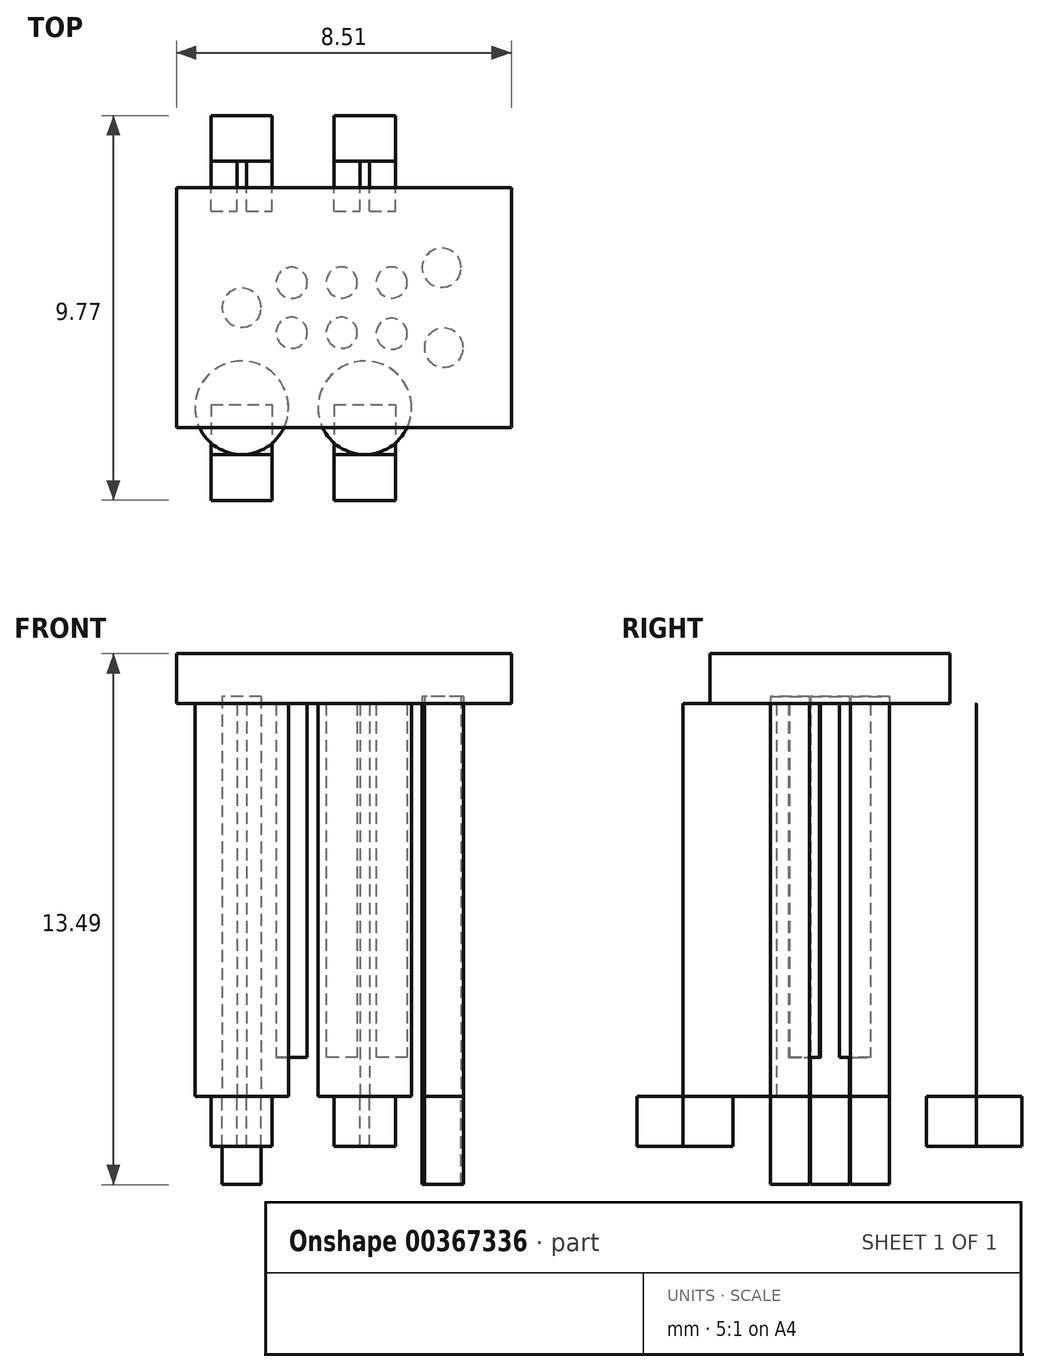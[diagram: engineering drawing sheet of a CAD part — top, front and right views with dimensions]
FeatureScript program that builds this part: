
annotation { "Feature Type Name" : "Feature", "Feature Type Description" : "" }
export const myFeature = defineFeature(function(context is Context, id is Id, definition is map)
    precondition{}
    {
        {
            var Q0;
            Q0=qCreatedBy(makeId("Top.planeOp"),FACE);
            var sketch = newSketch(context, id + "F0", { "sketchPlane" : qUnion([Q0])});
            skCircle(sketch, "E0", {"center": v(0, 0) * mm, "radius": 0.5 * mm});
            skCircle(sketch, "E1", {"center": v(5.13, -1.02) * mm, "radius": 0.5 * mm});
            skCircle(sketch, "E2", {"center": v(5.08, 1.02) * mm, "radius": 0.5 * mm});
            skCircle(sketch, "E3", {"center": v(1.27, 0.64) * mm, "radius": 0.4 * mm});
            skCircle(sketch, "E4", {"center": v(1.27, -0.63) * mm, "radius": 0.4 * mm});
            skCircle(sketch, "E5", {"center": v(2.54, 0.64) * mm, "radius": 0.4 * mm});
            skCircle(sketch, "E6", {"center": v(2.54, -0.63) * mm, "radius": 0.4 * mm});
            skCircle(sketch, "E7", {"center": v(3.81, 0.64) * mm, "radius": 0.4 * mm});
            skCircle(sketch, "E8", {"center": v(3.81, -0.66) * mm, "radius": 0.4 * mm});
            skCircle(sketch, "E9", {"center": v(0, 2.54) * mm, "radius": 1.19 * mm});
            skCircle(sketch, "E10", {"center": v(3.13, 2.54) * mm, "radius": 1.19 * mm});
            skCircle(sketch, "E11", {"center": v(0, -2.54) * mm, "radius": 1.19 * mm});
            skCircle(sketch, "E12", {"center": v(3.13, -2.54) * mm, "radius": 1.19 * mm});
            skLineSegment(sketch, "E13.bottom", {"start": v(-0.77, 4.88) * mm, "end": v(0.77, 4.88) * mm});
            skLineSegment(sketch, "E13.top", {"start": v(-0.77, 3.72) * mm, "end": v(0.77, 3.72) * mm});
            skLineSegment(sketch, "E13.left", {"start": v(-0.77, 4.88) * mm, "end": v(-0.77, 3.72) * mm});
            skLineSegment(sketch, "E13.right", {"start": v(0.77, 4.88) * mm, "end": v(0.77, 3.72) * mm});
            skLineSegment(sketch, "E14.bottom", {"start": v(2.35, 4.88) * mm, "end": v(3.9, 4.88) * mm});
            skLineSegment(sketch, "E14.top", {"start": v(2.35, 3.72) * mm, "end": v(3.9, 3.72) * mm});
            skLineSegment(sketch, "E14.left", {"start": v(2.35, 4.88) * mm, "end": v(2.35, 3.72) * mm});
            skLineSegment(sketch, "E14.right", {"start": v(3.9, 4.88) * mm, "end": v(3.9, 3.72) * mm});
            skLineSegment(sketch, "E15.bottom", {"start": v(-0.77, -3.73) * mm, "end": v(0.77, -3.73) * mm});
            skLineSegment(sketch, "E15.top", {"start": v(-0.77, -4.9) * mm, "end": v(0.77, -4.9) * mm});
            skLineSegment(sketch, "E15.left", {"start": v(-0.77, -3.73) * mm, "end": v(-0.77, -4.9) * mm});
            skLineSegment(sketch, "E15.right", {"start": v(0.77, -3.73) * mm, "end": v(0.77, -4.9) * mm});
            skLineSegment(sketch, "E16.bottom", {"start": v(2.35, -3.73) * mm, "end": v(3.9, -3.73) * mm});
            skLineSegment(sketch, "E16.top", {"start": v(2.35, -4.9) * mm, "end": v(3.9, -4.9) * mm});
            skLineSegment(sketch, "E16.left", {"start": v(2.35, -3.73) * mm, "end": v(2.35, -4.9) * mm});
            skLineSegment(sketch, "E16.right", {"start": v(3.9, -3.73) * mm, "end": v(3.9, -4.9) * mm});
            skSolve(sketch);
        }
        {
            var Q0;
            Q0=makeQuery(id+"F0.imprint","IMPRINT",FACE,{"disambiguationData":[TD([[makeQuery(id+"F0.imprint","IMPRINT",EDGE,{"derivedFrom":sQuery(id+"F0.wireOp",EDGE,"E13.bottom")}),-1.0]])]});
            var Q1;
            Q1=makeQuery(id+"F0.imprint","IMPRINT",FACE,{"disambiguationData":[TD([[makeQuery(id+"F0.imprint","IMPRINT",EDGE,{"derivedFrom":sQuery(id+"F0.wireOp",EDGE,"E14.bottom")}),-1.0]])]});
            var Q2;
            Q2=makeQuery(id+"F0.imprint","IMPRINT",FACE,{"disambiguationData":[TD([[makeQuery(id+"F0.imprint","IMPRINT",EDGE,{"derivedFrom":sQuery(id+"F0.wireOp",EDGE,"E15.bottom")}),-1.0]])]});
            var Q3;
            Q3=makeQuery(id+"F0.imprint","IMPRINT",FACE,{"disambiguationData":[TD([[makeQuery(id+"F0.imprint","IMPRINT",EDGE,{"derivedFrom":sQuery(id+"F0.wireOp",EDGE,"E16.bottom")}),-1.0]])]});
            extrude(context, id + "F1", {"entities" : qUnion([Q0, Q1, Q2, Q3]), "depth" : -1.27 * mm});
        }
        {
            var Q0;
            Q0=makeQuery(id+"F0.imprint","IMPRINT",FACE,{"disambiguationData":[TD([[makeQuery(id+"F0.imprint","IMPRINT",EDGE,{"derivedFrom":sQuery(id+"F0.wireOp",EDGE,"E1")}),1.0]])]});
            var Q1;
            Q1=makeQuery(id+"F0.imprint","IMPRINT",FACE,{"disambiguationData":[TD([[makeQuery(id+"F0.imprint","IMPRINT",EDGE,{"derivedFrom":sQuery(id+"F0.wireOp",EDGE,"E2")}),1.0]])]});
            var Q2;
            Q2=makeQuery(id+"F0.imprint","IMPRINT",FACE,{"disambiguationData":[TD([[makeQuery(id+"F0.imprint","IMPRINT",EDGE,{"derivedFrom":sQuery(id+"F0.wireOp",EDGE,"E0")}),1.0]])]});
            extrude(context, id + "F2", {"entities" : qUnion([Q0, Q1, Q2]), "depth" : -2.24 * mm});
        }
        {
            var Q0;
            Q0=makeQuery(id+"F0.imprint","IMPRINT",FACE,{"disambiguationData":[TD([[makeQuery(id+"F0.imprint","IMPRINT",EDGE,{"derivedFrom":sQuery(id+"F0.wireOp",EDGE,"E11")}),1.0]])]});
            var Q1;
            Q1=makeQuery(id+"F0.imprint","IMPRINT",FACE,{"disambiguationData":[TD([[makeQuery(id+"F0.imprint","IMPRINT",EDGE,{"derivedFrom":sQuery(id+"F0.wireOp",EDGE,"E12")}),1.0]])]});
            var Q2;
            {var subQ0=sQuery(id+"F0.wireOp",EDGE,"E14.top");var subQ1=sQuery(id+"F0.wireOp",EDGE,"E10");var subQ2=makeQuery(id+"F0.imprint","INTERSECT",VERTEX,{"disambiguationData":[OD(0.0)],"derivedFrom":[subQ1,subQ0]});Q2=makeQuery(id+"F0.imprint","IMPRINT",FACE,{"disambiguationData":[TD([[makeQuery(id+"F0.imprint","IMPRINT",EDGE,{"disambiguationData":[TD([[subQ2,-1.0]])],"derivedFrom":subQ1}),1.0]])]});}
            var Q3;
            {var subQ0=sQuery(id+"F0.wireOp",EDGE,"E13.top");var subQ1=sQuery(id+"F0.wireOp",EDGE,"E9");var subQ2=makeQuery(id+"F0.imprint","INTERSECT",VERTEX,{"disambiguationData":[OD(0.0)],"derivedFrom":[subQ1,subQ0]});Q3=makeQuery(id+"F0.imprint","IMPRINT",FACE,{"disambiguationData":[TD([[makeQuery(id+"F0.imprint","IMPRINT",EDGE,{"disambiguationData":[TD([[subQ2,-1.0]])],"derivedFrom":subQ1}),1.0]])]});}
            extrude(context, id + "F3", {"entities" : qUnion([Q0, Q1, Q2, Q3]), "depth" : 9.98 * mm});
        }
        {
            var Q0;
            {var subQ0=sQuery(id+"F0.wireOp",EDGE,"E13.top");Q0=makeQuery(id+"F1.opExtrude","SWEPT_FACE",FACE,{"disambiguationData":[OSD([subQ0]),TDD([makeQuery(id+"F0.imprint","IMPRINT",EDGE,{"disambiguationData":[TD([[makeQuery(id+"F0.imprint","INTERSECT",VERTEX,{"derivedFrom":[subQ0,sQuery(id+"F0.wireOp",EDGE,"E13.right")]}),1.0]])],"derivedFrom":subQ0})])]});}
            var Q1;
            {var subQ0=sQuery(id+"F0.wireOp",EDGE,"E13.top");Q1=makeQuery(id+"F1.opExtrude","SWEPT_FACE",FACE,{"disambiguationData":[OSD([subQ0]),TDD([makeQuery(id+"F0.imprint","IMPRINT",EDGE,{"disambiguationData":[TD([[makeQuery(id+"F0.imprint","INTERSECT",VERTEX,{"derivedFrom":[subQ0,sQuery(id+"F0.wireOp",EDGE,"E13.left")]}),-1.0]])],"derivedFrom":subQ0})])]});}
            var Q2;
            {var subQ0=sQuery(id+"F0.wireOp",EDGE,"E14.top");Q2=makeQuery(id+"F1.opExtrude","SWEPT_FACE",FACE,{"disambiguationData":[OSD([subQ0]),TDD([makeQuery(id+"F0.imprint","IMPRINT",EDGE,{"disambiguationData":[TD([[makeQuery(id+"F0.imprint","INTERSECT",VERTEX,{"derivedFrom":[subQ0,sQuery(id+"F0.wireOp",EDGE,"E14.left")]}),-1.0]])],"derivedFrom":subQ0})])]});}
            var Q3;
            {var subQ0=sQuery(id+"F0.wireOp",EDGE,"E14.top");Q3=makeQuery(id+"F1.opExtrude","SWEPT_FACE",FACE,{"disambiguationData":[OSD([subQ0]),TDD([makeQuery(id+"F0.imprint","IMPRINT",EDGE,{"disambiguationData":[TD([[makeQuery(id+"F0.imprint","INTERSECT",VERTEX,{"derivedFrom":[subQ0,sQuery(id+"F0.wireOp",EDGE,"E14.right")]}),1.0]])],"derivedFrom":subQ0})])]});}
            extrude(context, id + "F4", {"entities" : qUnion([Q0, Q1, Q2, Q3]), "depth" : 1.27 * mm});
        }
        {
            var Q0;
            Q0=makeQuery(id+"F1.opExtrude","SWEPT_FACE",FACE,{"disambiguationData":[OSD([sQuery(id+"F0.wireOp",EDGE,"E15.bottom")])]});
            var Q1;
            Q1=makeQuery(id+"F1.opExtrude","SWEPT_FACE",FACE,{"disambiguationData":[OSD([sQuery(id+"F0.wireOp",EDGE,"E16.bottom")])]});
            extrude(context, id + "F5", {"entities" : qUnion([Q0, Q1]), "depth" : 1.27 * mm});
        }
        {
            var Q0;
            Q0=makeQuery(id+"F0.imprint","IMPRINT",FACE,{"disambiguationData":[TD([[makeQuery(id+"F0.imprint","IMPRINT",EDGE,{"derivedFrom":sQuery(id+"F0.wireOp",EDGE,"E8")}),1.0]])]});
            var Q1;
            Q1=makeQuery(id+"F0.imprint","IMPRINT",FACE,{"disambiguationData":[TD([[makeQuery(id+"F0.imprint","IMPRINT",EDGE,{"derivedFrom":sQuery(id+"F0.wireOp",EDGE,"E7")}),1.0]])]});
            var Q2;
            Q2=makeQuery(id+"F0.imprint","IMPRINT",FACE,{"disambiguationData":[TD([[makeQuery(id+"F0.imprint","IMPRINT",EDGE,{"derivedFrom":sQuery(id+"F0.wireOp",EDGE,"E5")}),1.0]])]});
            var Q3;
            Q3=makeQuery(id+"F0.imprint","IMPRINT",FACE,{"disambiguationData":[TD([[makeQuery(id+"F0.imprint","IMPRINT",EDGE,{"derivedFrom":sQuery(id+"F0.wireOp",EDGE,"E6")}),1.0]])]});
            var Q4;
            Q4=makeQuery(id+"F0.imprint","IMPRINT",FACE,{"disambiguationData":[TD([[makeQuery(id+"F0.imprint","IMPRINT",EDGE,{"derivedFrom":sQuery(id+"F0.wireOp",EDGE,"E4")}),1.0]])]});
            var Q5;
            Q5=makeQuery(id+"F0.imprint","IMPRINT",FACE,{"disambiguationData":[TD([[makeQuery(id+"F0.imprint","IMPRINT",EDGE,{"derivedFrom":sQuery(id+"F0.wireOp",EDGE,"E3")}),1.0]])]});
            extrude(context, id + "F6", {"entities" : qUnion([Q0, Q1, Q2, Q3, Q4, Q5]), "depth" : 9.98 * mm, "hasSecondDirection" : true, "secondDirectionOppositeDirection" : true, "secondDirectionDepth" : -1 * mm});
        }
        {
            var Q0;
            Q0=makeQuery(id+"F3.opExtrude","CAP_FACE",FACE,{"disambiguationData":[OSD([sQuery(id+"F0.wireOp",EDGE,"E9"),sQuery(id+"F0.wireOp",EDGE,"E13.top")])],"isStart":false});
            var sketch = newSketch(context, id + "F7", { "sketchPlane" : qUnion([Q0])});
            skLineSegment(sketch, "E17.bottom", {"start": v(6.85, 3.05) * mm, "end": v(-1.66, 3.05) * mm});
            skLineSegment(sketch, "E17.top", {"start": v(6.85, -3.05) * mm, "end": v(-1.66, -3.05) * mm});
            skLineSegment(sketch, "E17.left", {"start": v(6.85, 3.05) * mm, "end": v(6.85, -3.05) * mm});
            skLineSegment(sketch, "E17.right", {"start": v(-1.66, 3.05) * mm, "end": v(-1.66, -3.05) * mm});
            skSolve(sketch);
        }
        {
            var Q0;
            Q0=makeQuery(id+"F7.imprint","IMPRINT",FACE,{"disambiguationData":[TD([[makeQuery(id+"F7.imprint","IMPRINT",EDGE,{"derivedFrom":sQuery(id+"F7.wireOp",EDGE,"E17.top")}),-1.0]])]});
            var Q1;
            {var subQ0=sQuery(id+"F7.wireOp",EDGE,"E17.bottom");var subQ1=makeQuery(id+"F3.opExtrude","CAP_EDGE",EDGE,{"disambiguationData":[OSD([sQuery(id+"F0.wireOp",EDGE,"E9")])],"isStart":false});var subQ2=makeQuery(id+"F7.imprint","INTERSECT",VERTEX,{"disambiguationData":[OD(0.0)],"derivedFrom":[subQ1,subQ0]});Q1=makeQuery(id+"F7.imprint","IMPRINT",FACE,{"disambiguationData":[TD([[makeQuery(id+"F7.imprint","IMPRINT",EDGE,{"disambiguationData":[TD([[subQ2,-1.0]])],"derivedFrom":subQ0}),1.0]])]});}
            extrude(context, id + "F8", {"entities" : qUnion([Q0, Q1]), "depth" : 1.27 * mm});
        }
        {
            var Q0;
            Q0=makeQuery(id+"F0.imprint","IMPRINT",FACE,{"disambiguationData":[TD([[makeQuery(id+"F0.imprint","IMPRINT",EDGE,{"derivedFrom":sQuery(id+"F0.wireOp",EDGE,"E0")}),1.0]])]});
            var Q1;
            Q1=makeQuery(id+"F0.imprint","IMPRINT",FACE,{"disambiguationData":[TD([[makeQuery(id+"F0.imprint","IMPRINT",EDGE,{"derivedFrom":sQuery(id+"F0.wireOp",EDGE,"E2")}),1.0]])]});
            var Q2;
            Q2=makeQuery(id+"F0.imprint","IMPRINT",FACE,{"disambiguationData":[TD([[makeQuery(id+"F0.imprint","IMPRINT",EDGE,{"derivedFrom":sQuery(id+"F0.wireOp",EDGE,"E1")}),1.0]])]});
            extrude(context, id + "F9", {"entities" : qUnion([Q0, Q1, Q2]), "depth" : 10.16 * mm});
        }
    });
